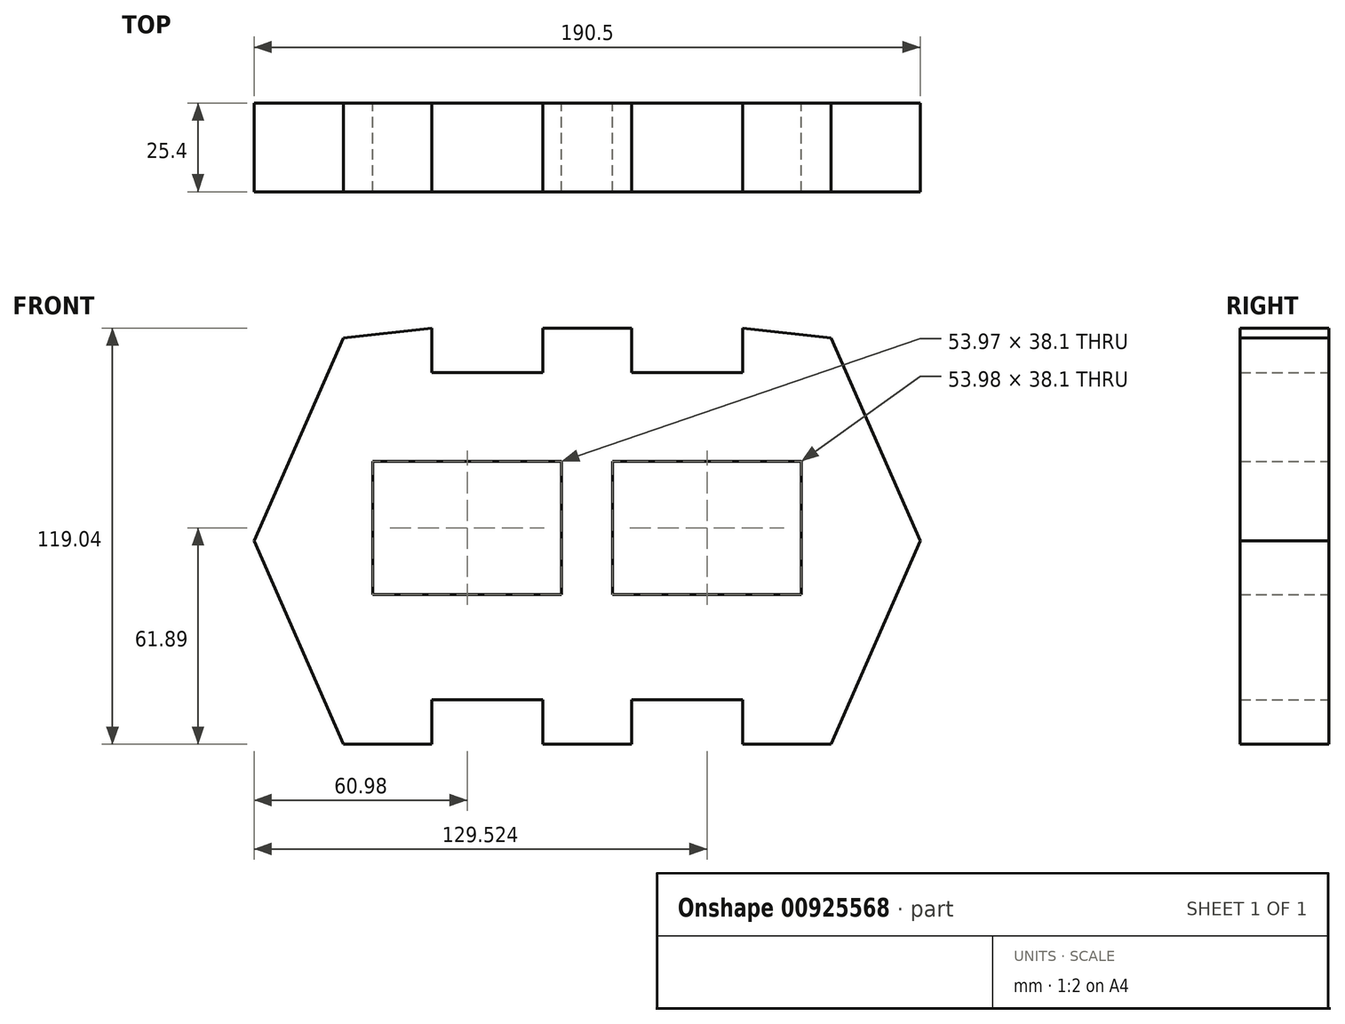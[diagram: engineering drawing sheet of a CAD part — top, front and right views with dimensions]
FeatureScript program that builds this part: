
annotation { "Feature Type Name" : "Feature", "Feature Type Description" : "" }
export const myFeature = defineFeature(function(context is Context, id is Id, definition is map)
    precondition{}
    {
        {
            var Q0;
            Q0=qCreatedBy(makeId("Front.planeOp"),FACE);
            var sketch = newSketch(context, id + "F0", { "sketchPlane" : qUnion([Q0])});
            skLineSegment(sketch, "E0", {"start": v(-54.95, 44.45) * mm, "end": v(-54.95, 57.15) * mm});
            skLineSegment(sketch, "E1", {"start": v(-54.95, 57.15) * mm, "end": v(-80.2, 54.38) * mm});
            skLineSegment(sketch, "E2", {"start": v(-80.2, 54.38) * mm, "end": v(-105.75, -3.76) * mm});
            skLineSegment(sketch, "E3", {"start": v(-105.75, -3.76) * mm, "end": v(-80.2, -61.89) * mm});
            skLineSegment(sketch, "E4.bottom", {"start": v(-71.76, 19.05) * mm, "end": v(-17.78, 19.05) * mm});
            skLineSegment(sketch, "E4.top", {"start": v(-71.76, -19.05) * mm, "end": v(-17.78, -19.05) * mm});
            skLineSegment(sketch, "E4.left", {"start": v(-71.76, 19.05) * mm, "end": v(-71.76, -19.05) * mm});
            skLineSegment(sketch, "E4.right", {"start": v(-17.78, 19.05) * mm, "end": v(-17.78, -19.05) * mm});
            skLineSegment(sketch, "E5", {"start": v(-80.2, -61.89) * mm, "end": v(-54.95, -61.89) * mm});
            skLineSegment(sketch, "E6", {"start": v(-54.95, -61.89) * mm, "end": v(-54.95, -49.19) * mm});
            skLineSegment(sketch, "E7", {"start": v(-54.95, -49.19) * mm, "end": v(-23.2, -49.19) * mm});
            skLineSegment(sketch, "E8", {"start": v(-23.2, -61.89) * mm, "end": v(3.04, -61.89) * mm});
            skLineSegment(sketch, "E9", {"start": v(-23.2, -61.89) * mm, "end": v(-23.2, -49.19) * mm});
            skLineSegment(sketch, "E10", {"start": v(-54.95, 44.45) * mm, "end": v(-23.2, 44.45) * mm});
            skLineSegment(sketch, "E11", {"start": v(-23.2, 44.45) * mm, "end": v(-23.2, 57.15) * mm});
            skLineSegment(sketch, "E12", {"start": v(-23.2, 57.15) * mm, "end": v(2.2, 57.15) * mm});
            skLineSegment(sketch, "E13", {"start": v(-10.5, 57.15) * mm, "end": v(-10.5, -61.89) * mm});
            skLineSegment(sketch, "E14.MirrorCS", {"start": v(2.2, 44.45) * mm, "end": v(2.2, 57.15) * mm});
            skLineSegment(sketch, "E15.MirrorCS", {"start": v(33.95, 44.45) * mm, "end": v(2.2, 44.45) * mm});
            skLineSegment(sketch, "E16.MirrorCS", {"start": v(33.95, 44.45) * mm, "end": v(33.95, 57.15) * mm});
            skLineSegment(sketch, "E17.MirrorCS", {"start": v(33.95, 57.15) * mm, "end": v(59.2, 54.38) * mm});
            skLineSegment(sketch, "E18.MirrorCS", {"start": v(59.2, 54.38) * mm, "end": v(84.75, -3.76) * mm});
            skLineSegment(sketch, "E19.MirrorCS", {"start": v(84.75, -3.76) * mm, "end": v(59.2, -61.89) * mm});
            skLineSegment(sketch, "E20.MirrorCS", {"start": v(59.2, -61.89) * mm, "end": v(33.95, -61.89) * mm});
            skLineSegment(sketch, "E21.MirrorCS", {"start": v(33.95, -61.89) * mm, "end": v(33.95, -49.19) * mm});
            skLineSegment(sketch, "E22.MirrorCS", {"start": v(33.95, -49.19) * mm, "end": v(2.2, -49.19) * mm});
            skLineSegment(sketch, "E23.MirrorCS", {"start": v(2.2, -61.89) * mm, "end": v(2.2, -49.19) * mm});
            skLineSegment(sketch, "E24.MirrorCS", {"start": v(-3.21, 19.05) * mm, "end": v(-3.21, -19.05) * mm});
            skLineSegment(sketch, "E25.MirrorCS", {"start": v(50.76, 19.05) * mm, "end": v(-3.21, 19.05) * mm});
            skLineSegment(sketch, "E26.MirrorCS", {"start": v(50.76, 19.05) * mm, "end": v(50.76, -19.05) * mm});
            skLineSegment(sketch, "E27.MirrorCS", {"start": v(50.76, -19.05) * mm, "end": v(-3.21, -19.05) * mm});
            skSolve(sketch);
        }
        {
            var Q0;
            Q0 = qSketchRegion(id + "F0", true);
            extrude(context, id + "F1", {"entities" : qUnion([Q0]), "depth" : 25.4 * mm, "offsetDistance" : 25.4 * mm});
        }
    });
